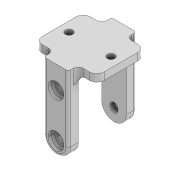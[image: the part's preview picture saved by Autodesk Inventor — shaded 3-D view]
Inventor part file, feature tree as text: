
AUTODESK INVENTOR PART (.ipt)
format: ipt  version: 2022 (Build 260153000, 153)  size: 268,800 bytes
history: native  units: mm
features: sketch x6, fillet x5, extrude x4, hole x2, projected_geometry x2, mirror x1
ambient origin geometry x8: Origin, YZ Plane, XZ Plane, XY Plane, X Axis, Y Axis, Z Axis, Center Point
bodies: Solid1 (feature_tree)
feature tree (20):
  extrude  "Extrusion1"  Depth=19.5mm
  extrude  "Extrusion2"  Depth=3.0mm
  extrude  "Extrusion3"  Depth=4.0mm TaperAngle=0.0deg
  extrude  "Extrusion4"  Depth=3.2mm
  hole  "Hole1"  [1 undecoded]
  mirror  "Mirror1"
  fillet  "Fillet1"  Radius=2.0mm
  fillet  "Fillet2"  Radius=1.0mm
  fillet  "Fillet3"  Radius=3.0mm
  fillet  "Fillet4"  Radius=4.0mm
  hole  "Hole2"  [1 undecoded]
  fillet  "Fillet5"  Radius=2.0mm
  sketch  "Sketch1"  dims[d0=25.0mm d1=19.5mm]
  sketch  "Sketch2"  dims[d2=3.0mm d3=0.0mm d4=27.0mm]
  sketch  "Sketch3"  dims[d5=10.0mm d6=4.0mm d7=0.0mm]
  sketch  "Sketch4"  dims[d9=0.5mm d10=3.2mm]
  sketch  "Sketch5"  dims[d11=3.0mm d12=0.0mm]
  sketch  "Sketch6"  dims[d14=3.2mm d15=6.0mm d16=6.3mm d17=2.0mm d18=90.0deg d19=5.0mm d20=20.594885mm d21=3.0mm d22=2.0mm d23=1.0mm d24=3.0mm d25=4.0mm d26=3.0mm d27=6.0mm d28=4.0mm d29=2.0mm d30=90.0deg d31=5.0mm d32=20.594885mm d33=6.3mm d34=2.0mm d35=0.0mm d36=0.7mm d37=18.0mm d8=1.0mm d13=0.375mm]
  projected_geometry  "Project Cut Edges1"
  projected_geometry  "Project Cut Edges2"
note: 2 required parameter values undecoded (feature->parameter linkage not recoverable at this tier; creation-order binding heuristic only, values carry confidence <= 0.55)
